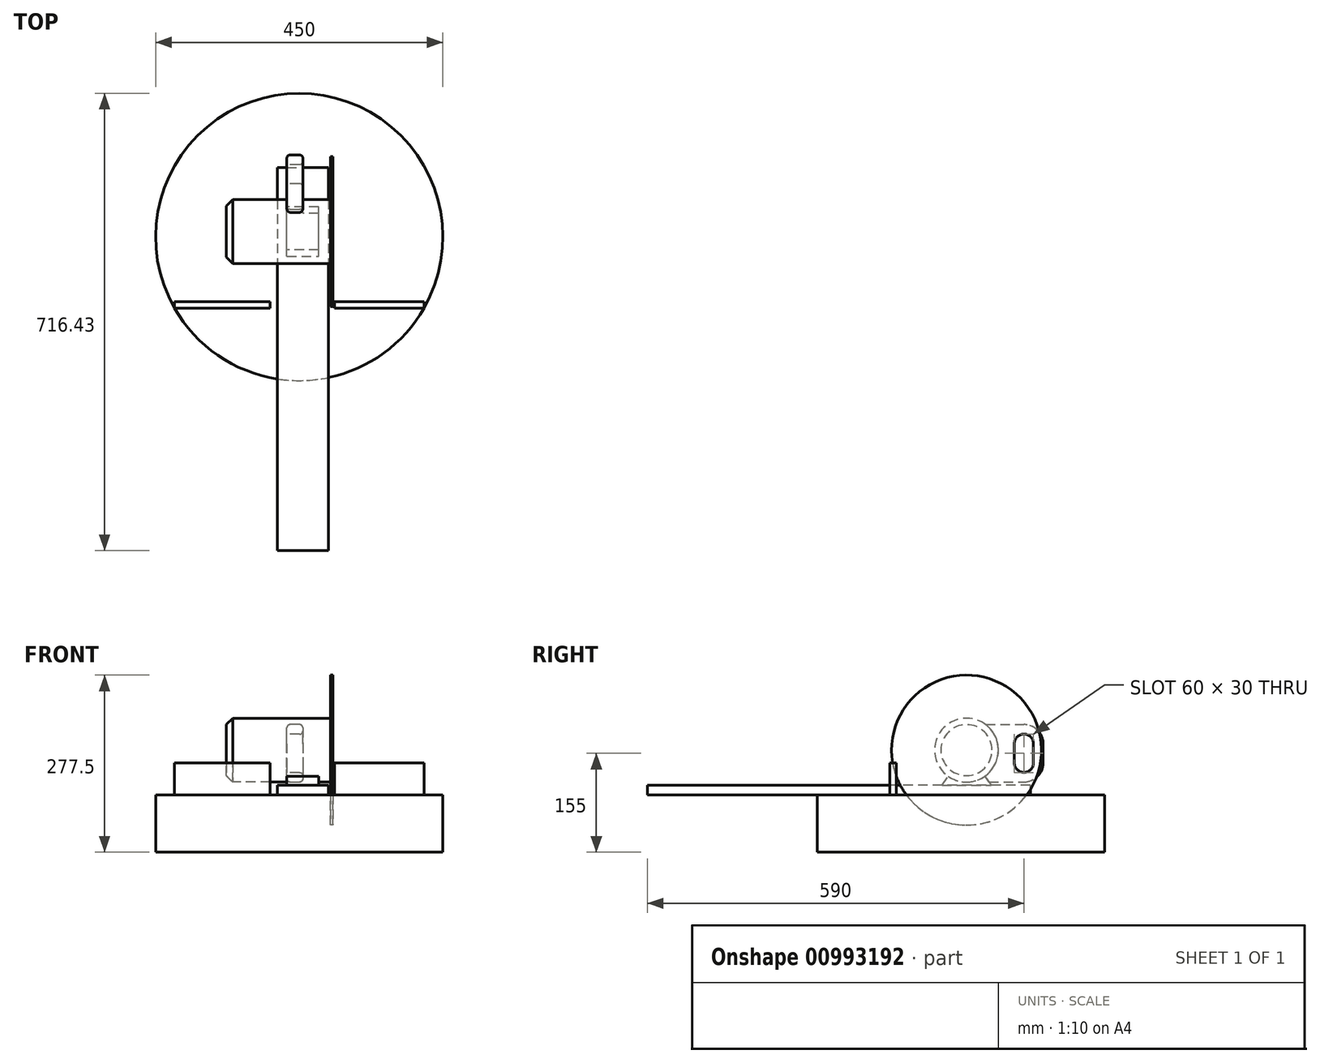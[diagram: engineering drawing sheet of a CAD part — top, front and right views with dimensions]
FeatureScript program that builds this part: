
annotation { "Feature Type Name" : "Feature", "Feature Type Description" : "" }
export const myFeature = defineFeature(function(context is Context, id is Id, definition is map)
    precondition{}
    {
        {
            var Q0;
            Q0=qCreatedBy(makeId("Top.planeOp"),FACE);
            var sketch = newSketch(context, id + "F0", { "sketchPlane" : qUnion([Q0])});
            skLineSegment(sketch, "E0.top", {"start": v(40, -500) * mm, "end": v(-40, -500) * mm});
            skLineSegment(sketch, "E0.left", {"start": v(40, 100) * mm, "end": v(40, -500) * mm});
            skLineSegment(sketch, "E0.right", {"start": v(-40, 100) * mm, "end": v(-40, -500) * mm});
            skPoint(sketch, "E0.middle", {"position": v(0, 0) * mm});
            skLineSegment(sketch, "E1", {"start": v(-40, 100) * mm, "end": v(40, 100) * mm});
            skSolve(sketch);
        }
        {
            var Q0;
            Q0=qSketchRegion(id+"F0",true);
            extrude(context, id + "F1", {"entities" : qUnion([Q0]), "oppositeDirection" : true, "depth" : 15 * mm, "offsetDistance" : 25 * mm});
        }
        {
            var Q0;
            Q0=qCreatedBy(makeId("Right.planeOp"),FACE);
            var sketch = newSketch(context, id + "F2", { "sketchPlane" : qUnion([Q0])});
            skLineSegment(sketch, "E2", {"start": v(0, 0) * mm, "end": v(0, 55) * mm, "construction": true});
            skCircle(sketch, "E3", {"center": v(0, 55) * mm, "radius": 50 * mm});
            skLineSegment(sketch, "E4", {"start": v(0, 55) * mm, "end": v(49.01, -15) * mm});
            skLineSegment(sketch, "E5", {"start": v(49.01, -15) * mm, "end": v(-49.01, -15) * mm});
            skLineSegment(sketch, "E6", {"start": v(-49.01, -15) * mm, "end": v(0, 55) * mm});
            skSolve(sketch);
        }
        {
            var Q0;
            Q0=makeQuery(id+"F2.imprint","IMPRINT",FACE,{"disambiguationData":[TD([[makeQuery(id+"F2.imprint","IMPRINT",EDGE,{"derivedFrom":sQuery(id+"F2.wireOp",EDGE,"E3")}),1.0]])]});
            var Q1;
            {var subQ0=sQuery(id+"F2.wireOp",EDGE,"E6");var subQ1=sQuery(id+"F2.wireOp",EDGE,"E3");var subQ2=makeQuery(id+"F2.imprint","INTERSECT",VERTEX,{"derivedFrom":[subQ1,subQ0]});Q1=makeQuery(id+"F2.imprint","IMPRINT",FACE,{"disambiguationData":[TD([[makeQuery(id+"F2.imprint","IMPRINT",EDGE,{"disambiguationData":[TD([[subQ2,1.0]])],"derivedFrom":subQ1}),1.0]])]});}
            extrude(context, id + "F3", {"entities" : qUnion([Q0, Q1]), "depth" : 43 * mm, "offsetDistance" : 25 * mm, "hasSecondDirection" : true, "secondDirectionOppositeDirection" : true, "secondDirectionDepth" : 120 * mm});
        }
        {
            var Q0;
            {var subQ5=sQuery(id+"F2.wireOp",EDGE,"E5");Q0=makeQuery(id+"F2.imprint","IMPRINT",FACE,{"disambiguationData":[TD([[makeQuery(id+"F2.imprint","IMPRINT",EDGE,{"derivedFrom":subQ5}),-1.0]])]});}
            extrude(context, id + "F4", {"entities" : qUnion([Q0]), "operationType" : NewBodyOperationType.ADD, "depth" : 25 * mm, "offsetDistance" : 25 * mm, "hasSecondDirection" : true, "secondDirectionOppositeDirection" : true, "secondDirectionDepth" : 25 * mm});
        }
        {
            var Q0;
            Q0=makeQuery(id+"F3.opExtrude","CAP_FACE",FACE,{"disambiguationData":[OSD([sQuery(id+"F2.wireOp",EDGE,"E3")])],"isStart":false});
            var sketch = newSketch(context, id + "F5", { "sketchPlane" : qUnion([Q0])});
            skCircle(sketch, "E7", {"center": v(0, 55) * mm, "radius": 117.5 * mm});
            skSolve(sketch);
        }
        {
            var Q0;
            Q0=qSketchRegion(id+"F5",true);
            extrude(context, id + "F6", {"entities" : qUnion([Q0]), "depth" : 4 * mm, "offsetDistance" : 25 * mm});
        }
        {
            var Q0;
            Q0=qCreatedBy(makeId("Front.planeOp"),FACE);
            cPlane(context, id + "F7", {"entities" : qUnion([Q0]), "cplaneType" : CPlaneType.OFFSET, "offset" : 120 * mm, "oppositeDirection" : true, "width" : 150 * mm, "height" : 150 * mm});
        }
        {
            var Q0;
            Q0=qCreatedBy(id+"F7.planeOp",FACE);
            var sketch = newSketch(context, id + "F8", { "sketchPlane" : qUnion([Q0])});
            skLineSegment(sketch, "E8.bottom", {"start": v(0, 5) * mm, "end": v(-25, 5) * mm});
            skLineSegment(sketch, "E8.top", {"start": v(0, 95) * mm, "end": v(-25, 95) * mm});
            skLineSegment(sketch, "E8.left", {"start": v(0, 5) * mm, "end": v(0, 95) * mm});
            skLineSegment(sketch, "E8.right", {"start": v(-25, 5) * mm, "end": v(-25, 95) * mm});
            skSolve(sketch);
        }
        {
            var Q0;
            Q0=qSketchRegion(id+"F8",true);
            extrude(context, id + "F9", {"entities" : qUnion([Q0]), "operationType" : NewBodyOperationType.ADD, "endBound" : BoundingType.UP_TO_NEXT, "depth" : 25 * mm, "offsetDistance" : 25 * mm});
        }
        {
            var Q0;
            Q0=makeQuery(id+"F9.opExtrude","CAP_EDGE",EDGE,{"disambiguationData":[OSD([sQuery(id+"F8.wireOp",EDGE,"E8.top")])],"isStart":true});
            var Q1;
            Q1=makeQuery(id+"F9.opExtrude","CAP_EDGE",EDGE,{"disambiguationData":[OSD([sQuery(id+"F8.wireOp",EDGE,"E8.bottom")])],"isStart":true});
            fillet(context, id + "F10", {"entities" : qUnion([Q0, Q1]), "radius" : 30 * mm, "tangentPropagation" : true, "allowEdgeOverflow" : false});
        }
        {
            var Q0;
            Q0=makeQuery(id+"F3.opExtrude","CAP_FACE",FACE,{"disambiguationData":[OSD([sQuery(id+"F2.wireOp",EDGE,"E3")])],"isStart":true});
            chamfer(context, id + "F11", {"entities" : qUnion([Q0]), "width" : 10 * mm, "tangentPropagation" : true});
        }
        {
            var Q0;
            Q0=makeQuery(id+"F9.boolean.opBoolean","MERGE",FACE,{"derivedFrom":[makeQuery(id+"F4.opExtrude","CAP_FACE",FACE,{"disambiguationData":[OSD([sQuery(id+"F2.wireOp",EDGE,"E3"),sQuery(id+"F2.wireOp",EDGE,"E5"),sQuery(id+"F2.wireOp",EDGE,"E6")])],"isStart":true}),makeQuery(id+"F9.opExtrude","SWEPT_FACE",FACE,{"disambiguationData":[OSD([sQuery(id+"F8.wireOp",EDGE,"E8.right")])]})]});
            var sketch = newSketch(context, id + "F12", { "sketchPlane" : qUnion([Q0])});
            skArc(sketch, "E9", {"start": v(-75, 65) * mm, "mid": v(-90, 80) * mm, "end": v(-105, 65) * mm});
            skArc(sketch, "E10", {"start": v(-105, 35) * mm, "mid": v(-90, 20) * mm, "end": v(-75, 35) * mm});
            skLineSegment(sketch, "E11", {"start": v(-105, 65) * mm, "end": v(-105, 35) * mm});
            skLineSegment(sketch, "E12", {"start": v(-75, 65) * mm, "end": v(-75, 35) * mm});
            skSolve(sketch);
        }
        {
            var Q0;
            Q0=makeQuery(id+"F12.imprint","IMPRINT",FACE,{"disambiguationData":[TD([[makeQuery(id+"F12.imprint","IMPRINT",EDGE,{"derivedFrom":sQuery(id+"F12.wireOp",EDGE,"E9")}),1.0]])]});
            extrude(context, id + "F13", {"entities" : qUnion([Q0]), "operationType" : NewBodyOperationType.REMOVE, "endBound" : BoundingType.THROUGH_ALL, "oppositeDirection" : true, "depth" : 25 * mm, "offsetDistance" : 25 * mm});
        }
        {
            var Q0;
            Q0=makeQuery(id+"F10.opFillet","BLEND_EDGE",EDGE,{"blendedFrom":[makeQuery(id+"F9.opExtrude","CAP_EDGE",EDGE,{"disambiguationData":[OSD([sQuery(id+"F8.wireOp",EDGE,"E8.top")])],"isStart":true}),makeQuery(id+"F9.boolean.opBoolean","MERGE",FACE,{"derivedFrom":[makeQuery(id+"F4.opExtrude","CAP_FACE",FACE,{"disambiguationData":[OSD([sQuery(id+"F2.wireOp",EDGE,"E3"),sQuery(id+"F2.wireOp",EDGE,"E5"),sQuery(id+"F2.wireOp",EDGE,"E6")])],"isStart":true}),makeQuery(id+"F9.opExtrude","SWEPT_FACE",FACE,{"disambiguationData":[OSD([sQuery(id+"F8.wireOp",EDGE,"E8.right")])]})]})],"blendedInto":[makeQuery(id+"F9.boolean.opBoolean","MERGE",FACE,{"derivedFrom":[makeQuery(id+"F4.opExtrude","CAP_FACE",FACE,{"disambiguationData":[OSD([sQuery(id+"F2.wireOp",EDGE,"E3"),sQuery(id+"F2.wireOp",EDGE,"E5"),sQuery(id+"F2.wireOp",EDGE,"E6")])],"isStart":true}),makeQuery(id+"F9.opExtrude","SWEPT_FACE",FACE,{"disambiguationData":[OSD([sQuery(id+"F8.wireOp",EDGE,"E8.right")])]})]})]});
            var Q1;
            Q1=makeQuery(id+"F13.boolean.opBoolean","COPY",EDGE,{"derivedFrom":makeQuery(id+"F13.opExtrude","CAP_EDGE",EDGE,{"disambiguationData":[OSD([sQuery(id+"F12.wireOp",EDGE,"E11")])],"isStart":true})});
            var Q2;
            Q2=makeQuery(id+"F9.opExtrude","CAP_EDGE",EDGE,{"disambiguationData":[OSD([sQuery(id+"F8.wireOp",EDGE,"E8.left")])],"isStart":true});
            var Q3;
            Q3=makeQuery(id+"F13.boolean.opBoolean","INTERSECT",EDGE,{"derivedFrom":[makeQuery(id+"F9.opExtrude","SWEPT_FACE",FACE,{"disambiguationData":[OSD([sQuery(id+"F8.wireOp",EDGE,"E8.left")])]}),makeQuery(id+"F13.opExtrude","SWEPT_FACE",FACE,{"disambiguationData":[OSD([sQuery(id+"F12.wireOp",EDGE,"E11")])]})]});
            fillet(context, id + "F14", {"entities" : qUnion([Q0, Q1, Q2, Q3]), "radius" : 5 * mm, "tangentPropagation" : true, "allowEdgeOverflow" : false});
        }
        {
            var Q0;
            Q0=makeQuery(id+"F1.opExtrude","CAP_FACE",FACE,{"disambiguationData":[OSD([sQuery(id+"F0.wireOp",EDGE,"E0.top"),sQuery(id+"F0.wireOp",EDGE,"E0.left"),sQuery(id+"F0.wireOp",EDGE,"E0.right"),sQuery(id+"F0.wireOp",EDGE,"E1")])],"isStart":false});
            var sketch = newSketch(context, id + "F15", { "sketchPlane" : qUnion([Q0])});
            skCircle(sketch, "E13", {"center": v(-5.65, 8.57) * mm, "radius": 225 * mm});
            skSolve(sketch);
        }
        {
            var Q0;
            Q0 = qSketchRegion(id + "F15", true);
            extrude(context, id + "F16", {"entities" : qUnion([Q0]), "depth" : 90 * mm, "offsetDistance" : 25 * mm});
        }
        {
            var Q0;
            Q0=makeQuery(id+"F16.opExtrude","CAP_FACE",FACE,{"disambiguationData":[OSD([sQuery(id+"F15.wireOp",EDGE,"E13")])],"isStart":true});
            var sketch = newSketch(context, id + "F17", { "sketchPlane" : qUnion([Q0])});
            skLineSegment(sketch, "E14.bottom", {"start": v(189.82, -120) * mm, "end": v(49.82, -120) * mm});
            skLineSegment(sketch, "E14.top", {"start": v(189.82, -110) * mm, "end": v(49.82, -110) * mm});
            skLineSegment(sketch, "E14.left", {"start": v(189.82, -120) * mm, "end": v(189.82, -110) * mm});
            skLineSegment(sketch, "E14.right", {"start": v(49.82, -120) * mm, "end": v(49.82, -110) * mm});
            skLineSegment(sketch, "E15.bottom", {"start": v(-201.11, -120) * mm, "end": v(-51.11, -120) * mm});
            skLineSegment(sketch, "E15.top", {"start": v(-201.11, -110) * mm, "end": v(-51.11, -110) * mm});
            skLineSegment(sketch, "E15.left", {"start": v(-201.11, -120) * mm, "end": v(-201.11, -110) * mm});
            skLineSegment(sketch, "E15.right", {"start": v(-51.11, -120) * mm, "end": v(-51.11, -110) * mm});
            skSolve(sketch);
        }
        {
            var Q0;
            Q0=makeQuery(id+"F17.imprint","IMPRINT",FACE,{"disambiguationData":[TD([[makeQuery(id+"F17.imprint","IMPRINT",EDGE,{"derivedFrom":sQuery(id+"F17.wireOp",EDGE,"E14.bottom")}),-1.0]])]});
            var Q1;
            Q1=makeQuery(id+"F17.imprint","IMPRINT",FACE,{"disambiguationData":[TD([[makeQuery(id+"F17.imprint","IMPRINT",EDGE,{"derivedFrom":sQuery(id+"F17.wireOp",EDGE,"E15.bottom")}),1.0]])]});
            extrude(context, id + "F18", {"entities" : qUnion([Q0, Q1]), "operationType" : NewBodyOperationType.ADD, "depth" : 50 * mm, "offsetDistance" : 25 * mm});
        }
    });
